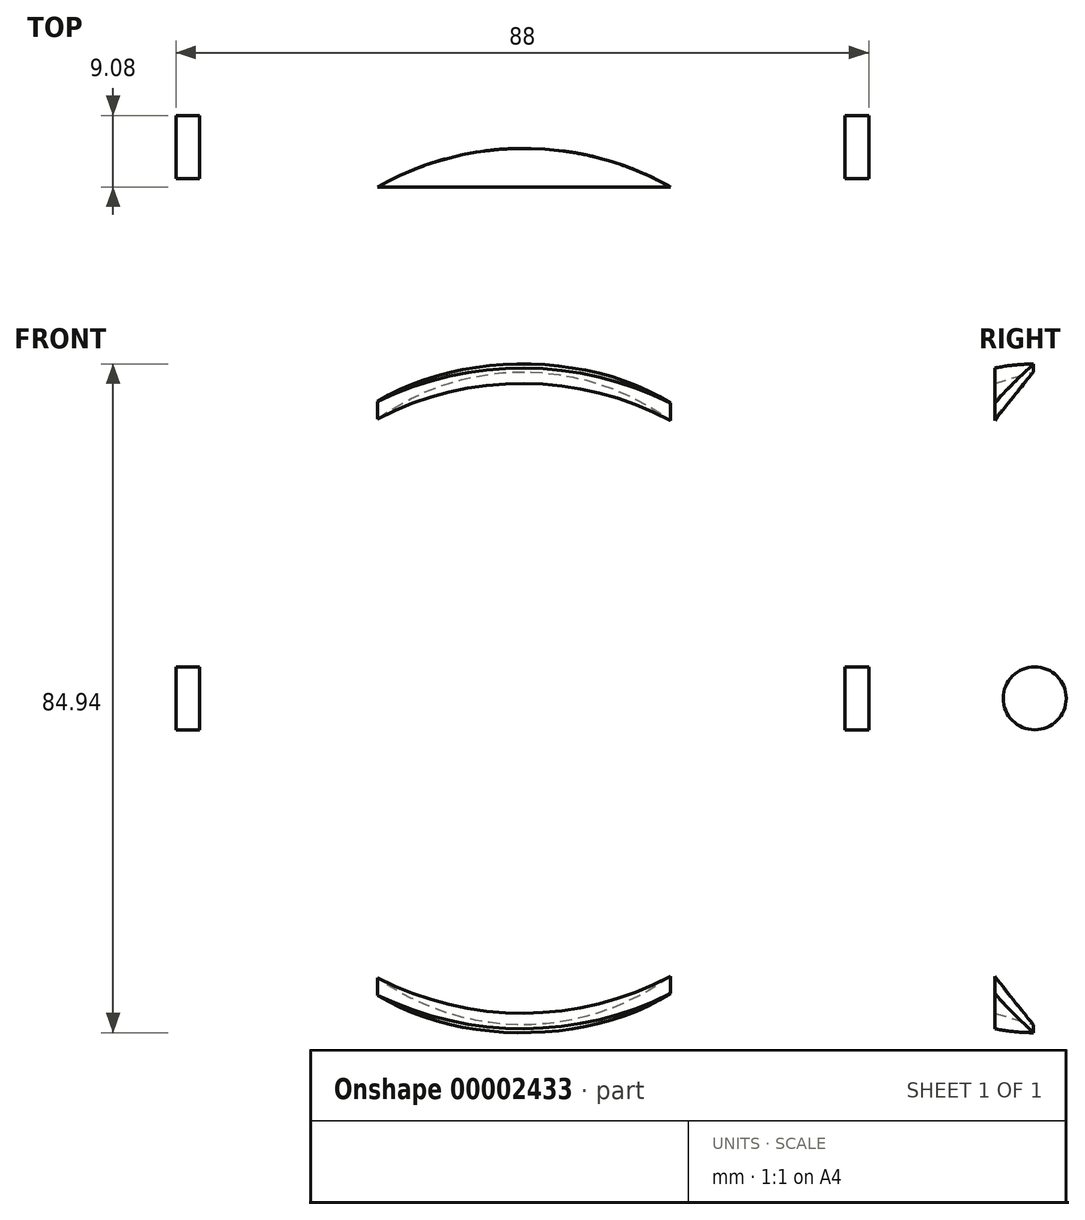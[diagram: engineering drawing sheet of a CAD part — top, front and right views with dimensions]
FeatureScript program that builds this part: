
annotation { "Feature Type Name" : "Feature", "Feature Type Description" : "" }
export const myFeature = defineFeature(function(context is Context, id is Id, definition is map)
    precondition{}
    {
        {
            var Q0;
            Q0=qCreatedBy(makeId("Top.planeOp"),FACE);
            var sketch = newSketch(context, id + "F0", { "sketchPlane" : qUnion([Q0])});
            skLineSegment(sketch, "E0", {"start": v(-33.75, 2.75) * mm, "end": v(-34.25, 2.75) * mm});
            skLineSegment(sketch, "E1.bottom", {"start": v(-34.25, 11.25) * mm, "end": v(-36, 11.25) * mm});
            skLineSegment(sketch, "E1.top", {"start": v(-34.25, 6.25) * mm, "end": v(-36, 6.25) * mm});
            skLineSegment(sketch, "E1.right", {"start": v(-36, 11.25) * mm, "end": v(-36, 6.25) * mm});
            skLineSegment(sketch, "E2.bottom", {"start": v(-33.75, 11.25) * mm, "end": v(-32, 11.25) * mm});
            skLineSegment(sketch, "E2.top", {"start": v(-33.75, 6.25) * mm, "end": v(-32, 6.25) * mm});
            skLineSegment(sketch, "E2.right", {"start": v(-32, 11.25) * mm, "end": v(-32, 6.25) * mm});
            skLineSegment(sketch, "E3", {"start": v(-41.5, 16) * mm, "end": v(-40, 16) * mm});
            skLineSegment(sketch, "E4", {"start": v(-40, 16) * mm, "end": v(-40, 9.75) * mm});
            skLineSegment(sketch, "E5", {"start": v(-40, 9.75) * mm, "end": v(-36.5, 6.25) * mm});
            skLineSegment(sketch, "E6", {"start": v(-36.5, 6.25) * mm, "end": v(-36.5, 9.75) * mm});
            skLineSegment(sketch, "E7", {"start": v(-36.5, 9.75) * mm, "end": v(-36.5, 11.5) * mm});
            skArc(sketch, "E8", {"start": v(-38, 18) * mm, "mid": v(-39.96, 17.37) * mm, "end": v(-41.5, 16) * mm});
            skLineSegment(sketch, "E9", {"start": v(-41.5, 16) * mm, "end": v(-41.5, 4.17) * mm});
            skLineSegment(sketch, "E10", {"start": v(-35.25, 2.5) * mm, "end": v(-35.25, 6) * mm});
            skLineSegment(sketch, "E11", {"start": v(-35.25, 6) * mm, "end": v(-36.25, 6) * mm});
            skLineSegment(sketch, "E12", {"start": v(-36.25, 6) * mm, "end": v(-40, 9.75) * mm});
            skLineSegment(sketch, "E13", {"start": v(-40, 9.75) * mm, "end": v(-40, 16) * mm});
            skLineSegment(sketch, "E14", {"start": v(-33.75, 14.75) * mm, "end": v(-33.75, 11.25) * mm});
            skLineSegment(sketch, "E15", {"start": v(-34.25, 14.75) * mm, "end": v(-34.25, 11.25) * mm});
            skLineSegment(sketch, "E16", {"start": v(-34.25, 6.25) * mm, "end": v(-34.25, 11.25) * mm});
            skLineSegment(sketch, "E17", {"start": v(-33.75, 2.75) * mm, "end": v(-33.75, 6.25) * mm});
            skLineSegment(sketch, "E18", {"start": v(-33.75, 11.25) * mm, "end": v(-33.75, 6.25) * mm});
            skLineSegment(sketch, "E19", {"start": v(-34.25, 6.25) * mm, "end": v(-34.25, 2.75) * mm});
            skLineSegment(sketch, "E20", {"start": v(-41.5, 0) * mm, "end": v(41.5, 0) * mm, "construction": true});
            skLineSegment(sketch, "E21", {"start": v(-41.5, 4.17) * mm, "end": v(-41.5, 2.31) * mm});
            skLineSegment(sketch, "E22", {"start": v(-37.5, 0) * mm, "end": v(-31.45, 0) * mm});
            skLineSegment(sketch, "E23", {"start": v(-35.25, 2.5) * mm, "end": v(-32.75, 2.5) * mm});
            skLineSegment(sketch, "E24", {"start": v(-32.75, 2.5) * mm, "end": v(-32.75, 6) * mm});
            skLineSegment(sketch, "E25", {"start": v(-32.75, 6) * mm, "end": v(-31.45, 6) * mm});
            skLineSegment(sketch, "E26", {"start": v(0, 1) * mm, "end": v(0, 0) * mm});
            skLineSegment(sketch, "E27", {"start": v(-40, 9.75) * mm, "end": v(-36.5, 9.75) * mm, "construction": true});
            skLineSegment(sketch, "E28", {"start": v(-36.5, 6.25) * mm, "end": v(-36, 6.25) * mm, "construction": true});
            skLineSegment(sketch, "E29", {"start": v(-41.5, 0) * mm, "end": v(-41.5, 18) * mm, "construction": true});
            skLineSegment(sketch, "E30", {"start": v(-34.02, 15) * mm, "end": v(-34.02, 14.75) * mm, "construction": true});
            skLineSegment(sketch, "E31", {"start": v(-34, 2.75) * mm, "end": v(-34, 2.5) * mm, "construction": true});
            skLineSegment(sketch, "E32", {"start": v(-41.5, 4.17) * mm, "end": v(-40, 4.17) * mm});
            skLineSegment(sketch, "E33", {"start": v(-40, 4.17) * mm, "end": v(-37.12, 4.17) * mm});
            skLineSegment(sketch, "E34", {"start": v(-37.12, 2.5) * mm, "end": v(-37.12, 4.17) * mm});
            skLineSegment(sketch, "E35", {"start": v(-37.12, 2.5) * mm, "end": v(-35.25, 2.5) * mm});
            skLineSegment(sketch, "E36", {"start": v(-33.75, 2.5) * mm, "end": v(-33.75, 0) * mm, "construction": true});
            skLineSegment(sketch, "E37", {"start": v(-44.1, 18) * mm, "end": v(-44.1, 17) * mm, "construction": true});
            skLineSegment(sketch, "E38", {"start": v(-44.1, 17) * mm, "end": v(-44.1, 16) * mm, "construction": true});
            skLineSegment(sketch, "E39", {"start": v(-44.1, 2.5) * mm, "end": v(-44.1, 1) * mm, "construction": true});
            skLineSegment(sketch, "E40", {"start": v(-44.1, 16) * mm, "end": v(-44.1, 11.5) * mm, "construction": true});
            skLineSegment(sketch, "E41", {"start": v(-44.1, 4.17) * mm, "end": v(-44.1, 2.5) * mm, "construction": true});
            skLineSegment(sketch, "E42", {"start": v(-41.5, 21.17) * mm, "end": v(-38, 21.17) * mm, "construction": true});
            skLineSegment(sketch, "E43", {"start": v(-38, 21.17) * mm, "end": v(-35.25, 21.17) * mm, "construction": true});
            skLineSegment(sketch, "E44", {"start": v(-35.25, 21.17) * mm, "end": v(-32.75, 21.17) * mm, "construction": true});
            skLineSegment(sketch, "E45", {"start": v(-30, 21.17) * mm, "end": v(-24, 21.17) * mm, "construction": true});
            skLineSegment(sketch, "E46", {"start": v(-24, 21.17) * mm, "end": v(0, 21.17) * mm, "construction": true});
            skLineSegment(sketch, "E47", {"start": v(-33.75, 4.5) * mm, "end": v(-32.75, 4.5) * mm, "construction": true});
            skLineSegment(sketch, "E48", {"start": v(-34.25, 4.5) * mm, "end": v(-35.25, 4.5) * mm, "construction": true});
            skLineSegment(sketch, "E49", {"start": v(0, 0) * mm, "end": v(0, 18) * mm, "construction": true});
            skLineSegment(sketch, "E50", {"start": v(-34.75, 11.5) * mm, "end": v(-36.5, 11.5) * mm});
            skLineSegment(sketch, "E51", {"start": v(-33.75, 14.75) * mm, "end": v(-34.25, 14.75) * mm});
            skLineSegment(sketch, "E52", {"start": v(-44.1, 6) * mm, "end": v(-44.1, 4.17) * mm, "construction": true});
            skLineSegment(sketch, "E53", {"start": v(-44.1, 7.45) * mm, "end": v(-44.1, 6) * mm, "construction": true});
            skLineSegment(sketch, "E54", {"start": v(-44.1, 7.45) * mm, "end": v(-31.45, 7.45) * mm, "construction": true});
            skLineSegment(sketch, "E55", {"start": v(-44.1, 11.25) * mm, "end": v(-44.1, 7.45) * mm, "construction": true});
            skLineSegment(sketch, "E56", {"start": v(-44.1, 11.5) * mm, "end": v(-44.1, 11.25) * mm, "construction": true});
            skLineSegment(sketch, "E57", {"start": v(-47.67, 11.5) * mm, "end": v(-47.67, 6) * mm, "construction": true});
            skLineSegment(sketch, "E58", {"start": v(-30, 1) * mm, "end": v(0, 1) * mm});
            skLineSegment(sketch, "E59", {"start": v(-38, 18) * mm, "end": v(0, 18) * mm});
            skLineSegment(sketch, "E60", {"start": v(0, 18) * mm, "end": v(0, 15.37) * mm});
            skLineSegment(sketch, "E61", {"start": v(0, 15.37) * mm, "end": v(-37.45, 15.37) * mm});
            skLineSegment(sketch, "E62", {"start": v(-44.1, 1) * mm, "end": v(-44.1, 0) * mm, "construction": true});
            skLineSegment(sketch, "E63", {"start": v(-47.34, 0) * mm, "end": v(-47.34, 2.5) * mm, "construction": true});
            skArc(sketch, "E64", {"start": v(-41.5, 2.31) * mm, "mid": v(-39.8, 0.62) * mm, "end": v(-37.5, 0) * mm});
            skLineSegment(sketch, "E65", {"start": v(-32.75, 21.17) * mm, "end": v(-30, 21.17) * mm, "construction": true});
            skLineSegment(sketch, "E66", {"start": v(-36.5, 11.5) * mm, "end": v(-40, 11.5) * mm});
            skLineSegment(sketch, "E67", {"start": v(-36.5, 18) * mm, "end": v(-7.22, 18) * mm});
            skLineSegment(sketch, "E68", {"start": v(-7.22, 18) * mm, "end": v(-7.22, 19.47) * mm});
            skLineSegment(sketch, "E69", {"start": v(-41.5, 25.09) * mm, "end": v(-35.25, 25.09) * mm, "construction": true});
            skLineSegment(sketch, "E70", {"start": v(-37.45, 15.37) * mm, "end": v(-35.8, 15.37) * mm});
            skLineSegment(sketch, "E71", {"start": v(-35.8, 15.37) * mm, "end": v(-34.75, 14.31) * mm});
            skLineSegment(sketch, "E72", {"start": v(-34.75, 14.31) * mm, "end": v(-34.75, 11.5) * mm});
            skLineSegment(sketch, "E73", {"start": v(-31.45, 6) * mm, "end": v(-30, 4.55) * mm});
            skLineSegment(sketch, "E74", {"start": v(-31.45, 0) * mm, "end": v(0, 0) * mm});
            skLineSegment(sketch, "E75", {"start": v(-31.45, 0) * mm, "end": v(-31.45, 1) * mm});
            skLineSegment(sketch, "E76", {"start": v(-31.45, 1) * mm, "end": v(-30, 1) * mm});
            skLineSegment(sketch, "E77", {"start": v(-30, 4.55) * mm, "end": v(-30, 1) * mm});
            skLineSegment(sketch, "E78", {"start": v(-38, 18) * mm, "end": v(-37.45, 17.45) * mm});
            skArc(sketch, "E79", {"start": v(-41.5, 16) * mm, "mid": v(-42.23, 12.62) * mm, "end": v(-42.47, 9.17) * mm});
            skLineSegment(sketch, "E80", {"start": v(-41.5, 4.17) * mm, "end": v(-41.96, 4.17) * mm});
            skLineSegment(sketch, "E81", {"start": v(-42.47, -8.95) * mm, "end": v(-42.47, 16.16) * mm, "construction": true});
            skLineSegment(sketch, "E82", {"start": v(-37.45, 17.45) * mm, "end": v(-37.45, 15.37) * mm});
            skLineSegment(sketch, "E83", {"start": v(-46.37, 4.17) * mm, "end": v(-46.37, 9.17) * mm, "construction": true});
            skArc(sketch, "E84", {"start": v(-42.47, 9.17) * mm, "mid": v(-42.23, 5.7) * mm, "end": v(-41.5, 2.31) * mm});
            skLineSegment(sketch, "E85", {"start": v(-42.47, 9.17) * mm, "end": v(-46.37, 9.17) * mm, "construction": true});
            skLineSegment(sketch, "E86", {"start": v(-42.47, 9.17) * mm, "end": v(-41.5, 9.17) * mm});
            skLineSegment(sketch, "E87", {"start": v(-41.5, 9.17) * mm, "end": v(-40, 4.17) * mm});
            skSolve(sketch);
        }
        {
            var Q0;
            Q0=makeQuery(id+"F0.imprint","IMPRINT",FACE,{"disambiguationData":[TD([[makeQuery(id+"F0.imprint","IMPRINT",EDGE,{"derivedFrom":sQuery(id+"F0.wireOp",EDGE,"E21")}),1.0]])]});
            var Q1;
            {var subQ2=sQuery(id+"F0.wireOp",EDGE,"E21");Q1=makeQuery(id+"F0.imprint","IMPRINT",FACE,{"disambiguationData":[TD([[makeQuery(id+"F0.imprint","IMPRINT",EDGE,{"derivedFrom":subQ2}),-1.0]])]});}
            var Q2;
            Q2=sQuery(id+"F0.wireOp",EDGE,"E49");
            revolve(context, id + "F1", {"entities" : qUnion([Q0, Q1]), "axis" : qUnion([Q2]), "revolveType" : RevolveType.FULL});
        }
        {
            var Q0;
            {var subQ2=sQuery(id+"F0.wireOp",EDGE,"E3");Q0=makeQuery(id+"F0.imprint","IMPRINT",FACE,{"disambiguationData":[TD([[makeQuery(id+"F0.imprint","IMPRINT",EDGE,{"derivedFrom":subQ2}),1.0]])]});}
            var Q1;
            {var subQ4=sQuery(id+"F0.wireOp",EDGE,"E6");Q1=makeQuery(id+"F0.imprint","IMPRINT",FACE,{"disambiguationData":[TD([[makeQuery(id+"F0.imprint","IMPRINT",EDGE,{"derivedFrom":subQ4}),1.0]])]});}
            var Q2;
            Q2=sQuery(id+"F0.wireOp",EDGE,"E49");
            revolve(context, id + "F2", {"entities" : qUnion([Q0, Q1]), "axis" : qUnion([Q2]), "revolveType" : RevolveType.FULL});
        }
        {
            var Q0;
            Q0=qCreatedBy(makeId("Top.planeOp"),FACE);
            var sketch = newSketch(context, id + "F3", { "sketchPlane" : qUnion([Q0])});
            skArc(sketch, "E88", {"start": v(18.81, 4.17) * mm, "mid": v(0.2, 9.07) * mm, "end": v(-18.4, 4.17) * mm});
            skLineSegment(sketch, "E89", {"start": v(-18.4, 4.17) * mm, "end": v(18.81, 4.17) * mm});
            skLineSegment(sketch, "E90", {"start": v(-18.4, 9.17) * mm, "end": v(18.81, 9.17) * mm, "construction": true});
            skLineSegment(sketch, "E91", {"start": v(-18.4, 4.17) * mm, "end": v(-18.4, 9.17) * mm, "construction": true});
            skLineSegment(sketch, "E92", {"start": v(18.81, 4.17) * mm, "end": v(18.81, 9.17) * mm, "construction": true});
            skLineSegment(sketch, "E93", {"start": v(-18.4, 9.07) * mm, "end": v(18.81, 9.07) * mm, "construction": true});
            skSolve(sketch);
        }
        {
            var Q0;
            {var subQ7=sQuery(id+"F0.wireOp",EDGE,"E3");Q0=makeQuery(id+"F0.imprint","IMPRINT",FACE,{"disambiguationData":[TD([[makeQuery(id+"F0.imprint","IMPRINT",EDGE,{"derivedFrom":subQ7}),-1.0]])]});}
            var Q1;
            {var subQ1=sQuery(id+"F0.wireOp",EDGE,"E79");Q1=makeQuery(id+"F0.imprint","IMPRINT",FACE,{"disambiguationData":[TD([[makeQuery(id+"F0.imprint","IMPRINT",EDGE,{"derivedFrom":subQ1}),1.0]])]});}
            var Q2;
            Q2=sQuery(id+"F0.wireOp",EDGE,"E49");
            revolve(context, id + "F4", {"entities" : qUnion([Q0, Q1]), "axis" : qUnion([Q2]), "revolveType" : RevolveType.FULL});
        }
        {
            var Q0;
            Q0=qCreatedBy(makeId("Top.planeOp"),FACE);
            var sketch = newSketch(context, id + "F5", { "sketchPlane" : qUnion([Q0])});
            skLineSegment(sketch, "E94", {"start": v(0, 15.36) * mm, "end": v(-36.32, 15.36) * mm});
            skLineSegment(sketch, "E95", {"start": v(-37.45, 15.37) * mm, "end": v(-37.45, 17.45) * mm, "construction": true});
            skLineSegment(sketch, "E96", {"start": v(-37.45, 17.45) * mm, "end": v(-37.32, 17.57) * mm, "construction": true});
            skLineSegment(sketch, "E97", {"start": v(-36.9, 18) * mm, "end": v(0, 18) * mm});
            skLineSegment(sketch, "E98", {"start": v(0, 18) * mm, "end": v(0, 15.36) * mm});
            skLineSegment(sketch, "E99", {"start": v(0, 18) * mm, "end": v(36.9, 18) * mm, "construction": true});
            skArc(sketch, "E100", {"start": v(36.9, 18) * mm, "mid": v(0, 19) * mm, "end": v(-36.9, 18.15) * mm, "construction": true});
            skLineSegment(sketch, "E101", {"start": v(-36.9, 19) * mm, "end": v(36.9, 19) * mm, "construction": true});
            skLineSegment(sketch, "E102", {"start": v(0, 18) * mm, "end": v(0, 19) * mm});
            skLineSegment(sketch, "E103", {"start": v(-36.32, 15.36) * mm, "end": v(-37.32, 15.37) * mm});
            skLineSegment(sketch, "E104", {"start": v(-36.32, 15.36) * mm, "end": v(-36.32, 16.87) * mm});
            skLineSegment(sketch, "E105", {"start": v(-36.32, 16.87) * mm, "end": v(0, 16.87) * mm});
            skLineSegment(sketch, "E106", {"start": v(-37.45, 15.37) * mm, "end": v(-39.45, 15.37) * mm});
            skLineSegment(sketch, "E107", {"start": v(-39.45, 15.37) * mm, "end": v(-39.45, 20.5) * mm});
            skLineSegment(sketch, "E108", {"start": v(-39.45, 20.5) * mm, "end": v(0, 20.5) * mm});
            skLineSegment(sketch, "E109", {"start": v(0, 20.5) * mm, "end": v(0, 19) * mm});
            skLineSegment(sketch, "E110", {"start": v(-39.45, 15.37) * mm, "end": v(-40.45, 15.37) * mm});
            skLineSegment(sketch, "E111", {"start": v(-40.45, 15.37) * mm, "end": v(-40.45, 13.87) * mm});
            skLineSegment(sketch, "E112", {"start": v(-40.45, 13.87) * mm, "end": v(0, 13.87) * mm});
            skLineSegment(sketch, "E113", {"start": v(0, 13.87) * mm, "end": v(0, 15.36) * mm});
            skLineSegment(sketch, "E114", {"start": v(-37.32, 17.57) * mm, "end": v(-36.9, 18) * mm});
            skLineSegment(sketch, "E115", {"start": v(-37.32, 15.37) * mm, "end": v(-37.45, 15.37) * mm});
            skLineSegment(sketch, "E116", {"start": v(-37.32, 17.57) * mm, "end": v(-37.32, 15.37) * mm});
            skLineSegment(sketch, "E117", {"start": v(-36.32, 15.36) * mm, "end": v(-36.32, 13.87) * mm});
            skSolve(sketch);
        }
        {
            var Q0;
            {var subQ5=sQuery(id+"F5.wireOp",EDGE,"E102");Q0=makeQuery(id+"F5.imprint","IMPRINT",FACE,{"disambiguationData":[TD([[makeQuery(id+"F5.imprint","IMPRINT",EDGE,{"derivedFrom":subQ5}),1.0]])]});}
            var Q1;
            {var subQ1=sQuery(id+"F5.wireOp",EDGE,"E108");Q1=makeQuery(id+"F5.imprint","IMPRINT",FACE,{"disambiguationData":[TD([[makeQuery(id+"F5.imprint","IMPRINT",EDGE,{"derivedFrom":subQ1}),-1.0]])]});}
            var Q2;
            Q2=sQuery(id+"F5.wireOp",EDGE,"E109");
            revolve(context, id + "F6", {"entities" : qUnion([Q0, Q1]), "axis" : qUnion([Q2]), "revolveType" : RevolveType.FULL});
        }
        {
            var Q0;
            {var subQ2=sQuery(id+"F5.wireOp",EDGE,"E94");Q0=makeQuery(id+"F5.imprint","IMPRINT",FACE,{"disambiguationData":[TD([[makeQuery(id+"F5.imprint","IMPRINT",EDGE,{"derivedFrom":subQ2}),-1.0]])]});}
            var Q1;
            Q1=makeQuery(id+"F5.imprint","IMPRINT",FACE,{"disambiguationData":[TD([[makeQuery(id+"F5.imprint","IMPRINT",EDGE,{"derivedFrom":sQuery(id+"F5.wireOp",EDGE,"E94")}),1.0]])]});
            var Q2;
            Q2=makeQuery(id+"F5.imprint","IMPRINT",FACE,{"disambiguationData":[TD([[makeQuery(id+"F5.imprint","IMPRINT",EDGE,{"derivedFrom":sQuery(id+"F5.wireOp",EDGE,"E103")}),1.0]])]});
            var Q3;
            Q3=sQuery(id+"F5.wireOp",EDGE,"E98");
            revolve(context, id + "F7", {"entities" : qUnion([Q0, Q1, Q2]), "axis" : qUnion([Q3]), "revolveType" : RevolveType.FULL});
        }
        {
            var Q0;
            {var subQ1=sQuery(id+"F0.wireOp",EDGE,"E32");Q0=makeQuery(id+"F0.imprint","IMPRINT",FACE,{"disambiguationData":[TD([[makeQuery(id+"F0.imprint","IMPRINT",EDGE,{"derivedFrom":subQ1}),1.0]])]});}
            var Q1;
            {var subQ2=sQuery(id+"F0.wireOp",EDGE,"E80");Q1=makeQuery(id+"F0.imprint","IMPRINT",FACE,{"disambiguationData":[TD([[makeQuery(id+"F0.imprint","IMPRINT",EDGE,{"derivedFrom":subQ2}),-1.0]])]});}
            var Q2;
            Q2=sQuery(id+"F0.wireOp",EDGE,"E49");
            revolve(context, id + "F8", {"entities" : qUnion([Q0, Q1]), "axis" : qUnion([Q2]), "revolveType" : RevolveType.FULL});
        }
        {
            var Q0;
            Q0=makeQuery(id+"F3.imprint","IMPRINT",FACE,{"disambiguationData":[TD([[makeQuery(id+"F3.imprint","IMPRINT",EDGE,{"derivedFrom":sQuery(id+"F3.wireOp",EDGE,"E88")}),1.0]])]});
            extrude(context, id + "F9", {"entities" : qUnion([Q0]), "operationType" : NewBodyOperationType.REMOVE, "endBound" : BoundingType.SYMMETRIC, "depth" : 88.51 * mm});
        }
        {
            var Q0;
            {var subQ2=sQuery(id+"F0.wireOp",EDGE,"E80");Q0=makeQuery(id+"F0.imprint","IMPRINT",FACE,{"disambiguationData":[TD([[makeQuery(id+"F0.imprint","IMPRINT",EDGE,{"derivedFrom":subQ2}),-1.0]])]});}
            var Q1;
            {var subQ1=sQuery(id+"F0.wireOp",EDGE,"E32");Q1=makeQuery(id+"F0.imprint","IMPRINT",FACE,{"disambiguationData":[TD([[makeQuery(id+"F0.imprint","IMPRINT",EDGE,{"derivedFrom":subQ1}),1.0]])]});}
            var Q2;
            Q2=sQuery(id+"F0.wireOp",EDGE,"E49");
            revolve(context, id + "F10", {"entities" : qUnion([Q0, Q1]), "axis" : qUnion([Q2]), "revolveType" : RevolveType.FULL});
        }
        {
            var Q0;
            Q0=makeQuery(id+"F3.imprint","IMPRINT",FACE,{"disambiguationData":[TD([[makeQuery(id+"F3.imprint","IMPRINT",EDGE,{"derivedFrom":sQuery(id+"F3.wireOp",EDGE,"E88")}),1.0]])]});
            extrude(context, id + "F11", {"entities" : qUnion([Q0]), "operationType" : NewBodyOperationType.INTERSECT, "endBound" : BoundingType.SYMMETRIC, "oppositeDirection" : true, "depth" : 94.84 * mm});
        }
        {
            var Q0;
            Q0=qCreatedBy(makeId("Right.planeOp"),FACE);
            var sketch = newSketch(context, id + "F12", { "sketchPlane" : qUnion([Q0])});
            skLineSegment(sketch, "E118", {"start": v(0, 0) * mm, "end": v(0, 0) * mm});
            skLineSegment(sketch, "E119", {"start": v(2.5, -4.25) * mm, "end": v(16, -4.25) * mm, "construction": true});
            skLineSegment(sketch, "E120", {"start": v(2.5, -4.25) * mm, "end": v(2.5, 0) * mm, "construction": true});
            skLineSegment(sketch, "E121", {"start": v(16, 0) * mm, "end": v(16, -4.25) * mm, "construction": true});
            skLineSegment(sketch, "E122", {"start": v(16, 0) * mm, "end": v(2.5, 0) * mm, "construction": true});
            skCircle(sketch, "E123", {"center": v(9.25, 0) * mm, "radius": 4 * mm});
            skSolve(sketch);
        }
        {
            var Q0;
            Q0=makeQuery(id+"F12.imprint","IMPRINT",FACE,{"disambiguationData":[TD([[makeQuery(id+"F12.imprint","IMPRINT",EDGE,{"derivedFrom":sQuery(id+"F12.wireOp",EDGE,"E123")}),1.0]])]});
            extrude(context, id + "F13", {"entities" : qUnion([Q0]), "endBound" : BoundingType.SYMMETRIC, "depth" : 88 * mm});
        }
        {
            var Q0;
            Q0=makeQuery(id+"F12.imprint","IMPRINT",FACE,{"disambiguationData":[TD([[makeQuery(id+"F12.imprint","IMPRINT",EDGE,{"derivedFrom":sQuery(id+"F12.wireOp",EDGE,"E123")}),1.0]])]});
            extrude(context, id + "F14", {"entities" : qUnion([Q0]), "operationType" : NewBodyOperationType.REMOVE, "endBound" : BoundingType.SYMMETRIC, "depth" : 82 * mm});
        }
    });
